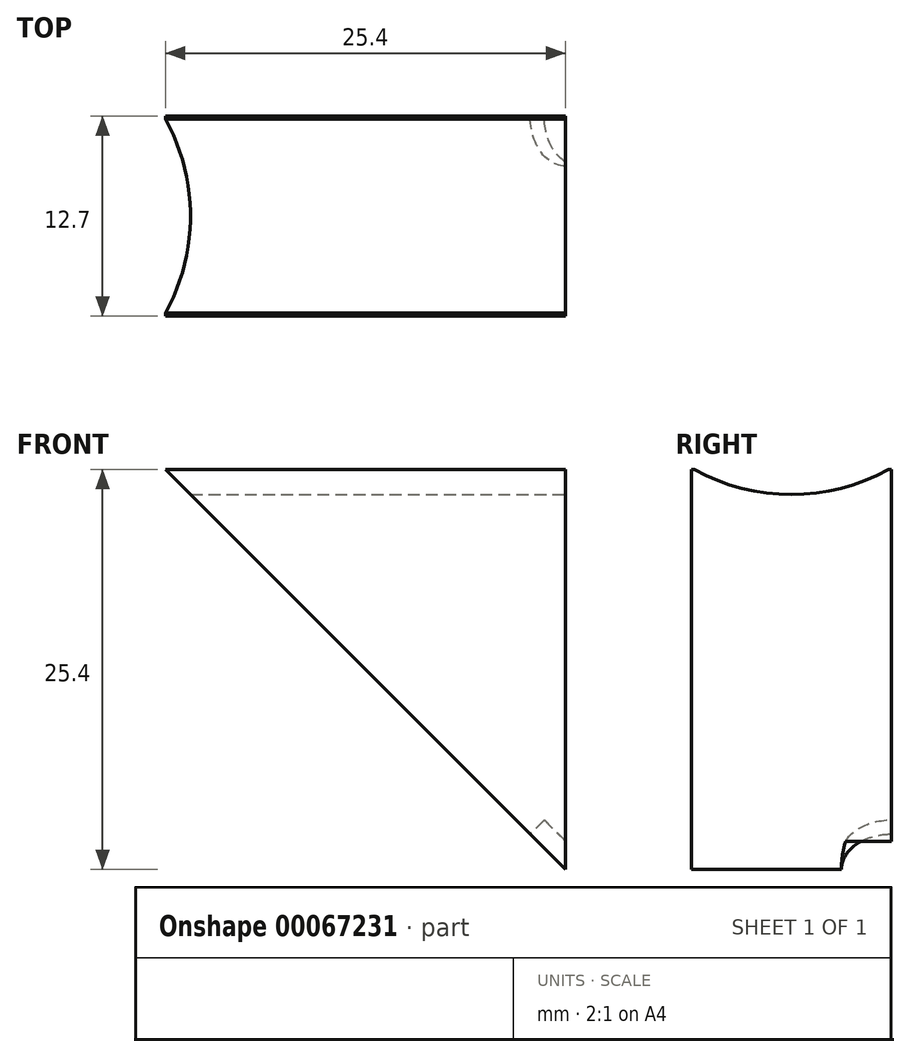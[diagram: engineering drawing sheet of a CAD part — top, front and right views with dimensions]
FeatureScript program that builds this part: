
annotation { "Feature Type Name" : "Feature", "Feature Type Description" : "" }
export const myFeature = defineFeature(function(context is Context, id is Id, definition is map)
    precondition{}
    {
        {
            var Q0;
            Q0=qCreatedBy(makeId("Front.planeOp"),FACE);
            var sketch = newSketch(context, id + "F0", { "sketchPlane" : qUnion([Q0])});
            skLineSegment(sketch, "E0", {"start": v(0, 0) * mm, "end": v(-25.4, 25.4) * mm});
            skLineSegment(sketch, "E1", {"start": v(-25.4, 25.4) * mm, "end": v(0, 25.4) * mm});
            skLineSegment(sketch, "E2", {"start": v(0, 25.4) * mm, "end": v(0, 0) * mm});
            skSolve(sketch);
        }
        {
            var Q0;
            Q0=makeQuery(id+"F0.imprint","IMPRINT",FACE,{"disambiguationData":[TD([[makeQuery(id+"F0.imprint","IMPRINT",EDGE,{"derivedFrom":sQuery(id+"F0.wireOp",EDGE,"E0")}),-1.0]])]});
            extrude(context, id + "F1", {"entities" : qUnion([Q0]), "depth" : 12.7 * mm, "symmetric" : true});
        }
        {
            var Q0;
            Q0=makeQuery(id+"F1.opExtrude","SWEPT_FACE",FACE,{"disambiguationData":[OSD([sQuery(id+"F0.wireOp",EDGE,"E0")])]});
            var sketch = newSketch(context, id + "F2", { "sketchPlane" : qUnion([Q0])});
            skCircle(sketch, "E3", {"center": v(-6.35, 0) * mm, "radius": 3.18 * mm});
            skCircle(sketch, "E4", {"center": v(-13.97, 0) * mm, "radius": 3.18 * mm});
            skSolve(sketch);
        }
        {
            var Q0;
            Q0=makeQuery(id+"F2.imprint","IMPRINT",FACE,{"disambiguationData":[TD([[makeQuery(id+"F2.imprint","IMPRINT",EDGE,{"derivedFrom":sQuery(id+"F2.wireOp",EDGE,"E4")}),1.0]])]});
            var Q1;
            Q1=makeQuery(id+"F2.imprint","IMPRINT",FACE,{"disambiguationData":[TD([[makeQuery(id+"F2.imprint","IMPRINT",EDGE,{"derivedFrom":sQuery(id+"F2.wireOp",EDGE,"E3")}),1.0]])]});
            extrude(context, id + "F3", {"entities" : qUnion([Q0, Q1]), "operationType" : NewBodyOperationType.REMOVE, "oppositeDirection" : true, "depth" : 1.27 * mm});
        }
        {
            var Q0;
            Q0=makeQuery(id+"F1.opExtrude","SWEPT_FACE",FACE,{"disambiguationData":[OSD([sQuery(id+"F0.wireOp",EDGE,"E2")])]});
            var sketch = newSketch(context, id + "F4", { "sketchPlane" : qUnion([Q0])});
            skCircle(sketch, "E5", {"center": v(0, 36.51) * mm, "radius": 12.7 * mm});
            skSolve(sketch);
        }
        {
            var Q0;
            {var subQ0=sQuery(id+"F4.wireOp",EDGE,"E5");var subQ1=makeQuery(id+"F1.opExtrude","SWEPT_EDGE",EDGE,{"disambiguationData":[OSD([sQuery(id+"F0.wireOp",EDGE,"E1"),sQuery(id+"F0.wireOp",EDGE,"E2")])]});var subQ2=makeQuery(id+"F4.imprint","INTERSECT",VERTEX,{"disambiguationData":[OD(0.0)],"derivedFrom":[subQ1,subQ0]});Q0=makeQuery(id+"F4.imprint","IMPRINT",FACE,{"disambiguationData":[TD([[makeQuery(id+"F4.imprint","IMPRINT",EDGE,{"disambiguationData":[TD([[subQ2,-1.0]])],"derivedFrom":subQ0}),1.0]])]});}
            var Q1;
            {var subQ0=sQuery(id+"F4.wireOp",EDGE,"E5");var subQ1=makeQuery(id+"F1.opExtrude","SWEPT_EDGE",EDGE,{"disambiguationData":[OSD([sQuery(id+"F0.wireOp",EDGE,"E1"),sQuery(id+"F0.wireOp",EDGE,"E2")])]});var subQ2=makeQuery(id+"F4.imprint","INTERSECT",VERTEX,{"disambiguationData":[OD(0.0)],"derivedFrom":[subQ1,subQ0]});Q1=makeQuery(id+"F4.imprint","IMPRINT",FACE,{"disambiguationData":[TD([[makeQuery(id+"F4.imprint","IMPRINT",EDGE,{"disambiguationData":[TD([[subQ2,1.0]])],"derivedFrom":subQ0}),1.0]])]});}
            extrude(context, id + "F5", {"entities" : qUnion([Q0, Q1]), "operationType" : NewBodyOperationType.REMOVE, "oppositeDirection" : true, "depth" : 25.4 * mm});
        }
    });
